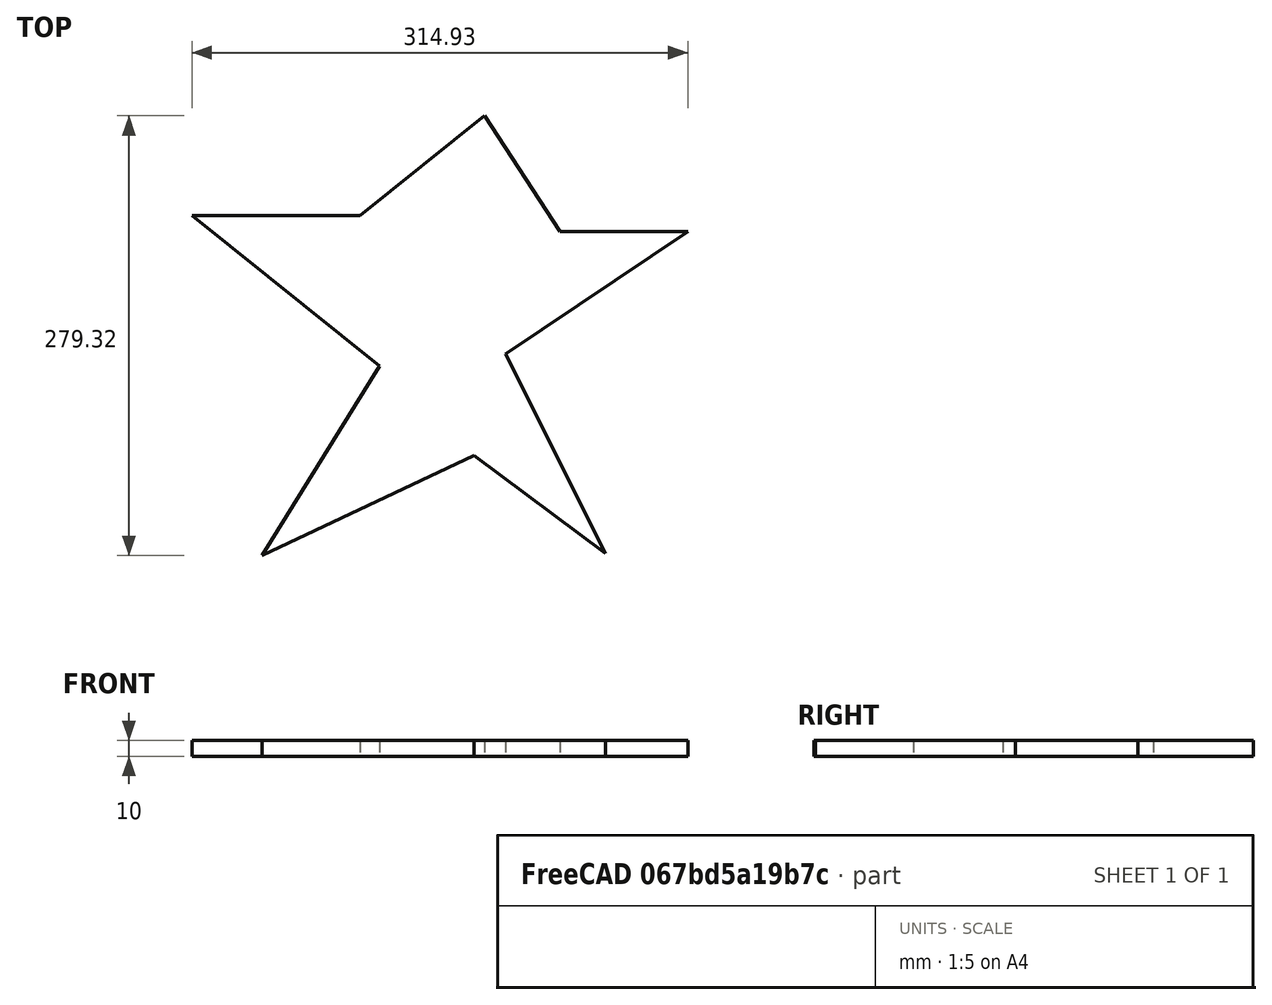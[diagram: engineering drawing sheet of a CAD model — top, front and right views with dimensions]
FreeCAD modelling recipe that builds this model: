
FCSTD DOCUMENT  (FreeCAD 0.19R)
Label: Board Star
License: All rights reserved
LicenseURL: http://en.wikipedia.org/wiki/All_rights_reserved
objects: Sketcher::SketchObject×1, PartDesign::Pad×1, PartDesign::Body×1
note: 4 computed .brp shape members not serialized (recipe doc carries the construction recipe); baked Part::Feature solids carry a one-line shape summary decoded from their .brp

FEATURE [Sketcher::SketchObject] Sketch  label="Board"
  FullyConstrained = false
  MapMode = 5
  Support = -> [XY_Plane]
  sketch-geometry (10):
    g0: LineSegment StartX=-38.6936 StartY=95.5216 StartZ=0 EndX=-117.703 EndY=32.0914 EndZ=0
    g1: LineSegment StartX=-117.703 StartY=32.0914 StartZ=0 EndX=-224.533 EndY=32.0914 EndZ=0
    g2: LineSegment StartX=-224.533 StartY=32.0914 StartZ=0 EndX=-105.462 EndY=-63.6102 EndZ=0
    g3: LineSegment StartX=-105.462 StartY=-63.6102 StartZ=0 EndX=-180.02 EndY=-183.794 EndZ=0
    g4: LineSegment StartX=-180.02 StartY=-183.794 StartZ=0 EndX=-45.3704 EndY=-120.363 EndZ=0
    g5: LineSegment StartX=-45.3704 StartY=-120.363 StartZ=0 EndX=38.0903 EndY=-182.681 EndZ=0
    g6: LineSegment StartX=38.0903 StartY=-182.681 StartZ=0 EndX=-25.3399 EndY=-55.8205 EndZ=0
    g7: LineSegment StartX=-25.3399 StartY=-55.8205 StartZ=0 EndX=90.3924 EndY=22.0761 EndZ=0
    g8: LineSegment StartX=90.3924 StartY=22.0761 StartZ=0 EndX=9.15726 EndY=22.0761 EndZ=0
    g9: LineSegment StartX=9.15726 StartY=22.0761 StartZ=0 EndX=-38.6936 EndY=95.5216 EndZ=0
  constraints (12):
    c: Coincident(g0,g1)
    c: Horizontal(g1)
    c: Coincident(g1,g2)
    c: Coincident(g2,g3)
    c: Coincident(g3,g4)
    c: Coincident(g4,g5)
    c: Coincident(g5,g6)
    c: Coincident(g6,g7)
    c: Coincident(g7,g8)
    c: Horizontal(g8)
    c: Coincident(g8,g9)
    c: Coincident(g9,g0)
FEATURE [PartDesign::Pad] Pad
  Direction = (1,1,1)
  Length = 10
  Length2 = 100
  Profile = -> Sketch
  Reversed = true
  Type = 0
FEATURE [PartDesign::Body] Body  label="Board Body"
  Group = -> [Sketch,Pad]
  Origin = -> Origin
  Placement = pos=(224.533,183.794,0) rot=(0,0,1;0rad)
  Tip = -> Pad
